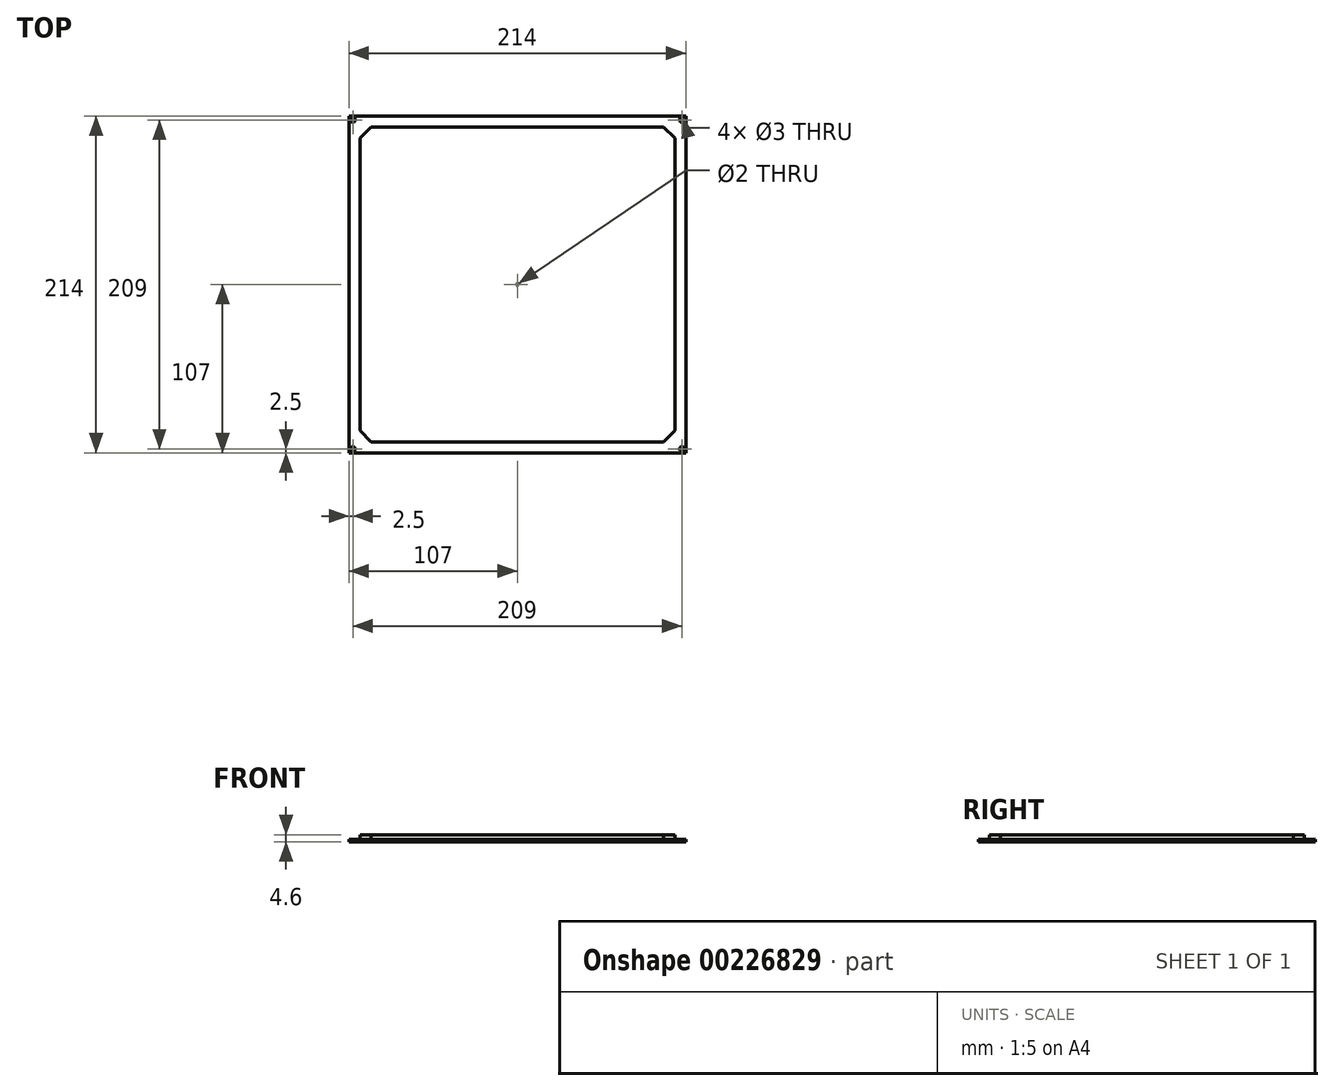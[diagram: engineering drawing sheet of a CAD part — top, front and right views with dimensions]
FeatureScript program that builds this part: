
annotation { "Feature Type Name" : "Feature", "Feature Type Description" : "" }
export const myFeature = defineFeature(function(context is Context, id is Id, definition is map)
    precondition{}
    {
        {
            var Q0;
            Q0=qCreatedBy(makeId("Top.planeOp"),FACE);
            var sketch = newSketch(context, id + "F0", { "sketchPlane" : qUnion([Q0])});
            skLineSegment(sketch, "E0.bottom", {"start": v(107, 107) * mm, "end": v(-107, 107) * mm});
            skLineSegment(sketch, "E0.top", {"start": v(107, -107) * mm, "end": v(-107, -107) * mm});
            skLineSegment(sketch, "E0.left", {"start": v(107, 107) * mm, "end": v(107, -107) * mm});
            skLineSegment(sketch, "E0.right", {"start": v(-107, 107) * mm, "end": v(-107, -107) * mm});
            skPoint(sketch, "E0.middle", {"position": v(0, 0) * mm});
            skLineSegment(sketch, "E1.bottom", {"start": v(104.5, 104.5) * mm, "end": v(-104.5, 104.5) * mm, "construction": true});
            skLineSegment(sketch, "E1.top", {"start": v(104.5, -104.5) * mm, "end": v(-104.5, -104.5) * mm, "construction": true});
            skLineSegment(sketch, "E1.left", {"start": v(104.5, 104.5) * mm, "end": v(104.5, -104.5) * mm, "construction": true});
            skLineSegment(sketch, "E1.right", {"start": v(-104.5, 104.5) * mm, "end": v(-104.5, -104.5) * mm, "construction": true});
            skCircle(sketch, "E2", {"center": v(-104.5, 104.5) * mm, "radius": 1.5 * mm});
            skCircle(sketch, "E3", {"center": v(104.5, 104.5) * mm, "radius": 1.5 * mm});
            skCircle(sketch, "E4", {"center": v(104.5, -104.5) * mm, "radius": 1.5 * mm});
            skCircle(sketch, "E5", {"center": v(-104.5, -104.5) * mm, "radius": 1.5 * mm});
            skCircle(sketch, "E6", {"center": v(0, 0) * mm, "radius": 1 * mm});
            skSolve(sketch);
        }
        {
            var Q0;
            Q0=makeQuery(id+"F0.imprint","IMPRINT",FACE,{"disambiguationData":[TD([[makeQuery(id+"F0.imprint","IMPRINT",EDGE,{"derivedFrom":sQuery(id+"F0.wireOp",EDGE,"E0.bottom")}),1.0]])]});
            extrude(context, id + "F1", {"entities" : qUnion([Q0]), "depth" : 1.6 * mm});
        }
        {
            var Q0;
            Q0=makeQuery(id+"F1.opExtrude","CAP_FACE",FACE,{"disambiguationData":[OSD([sQuery(id+"F0.wireOp",EDGE,"E0.bottom"),sQuery(id+"F0.wireOp",EDGE,"E0.top"),sQuery(id+"F0.wireOp",EDGE,"E0.left"),sQuery(id+"F0.wireOp",EDGE,"E0.right"),sQuery(id+"F0.wireOp",EDGE,"E2"),sQuery(id+"F0.wireOp",EDGE,"E3"),sQuery(id+"F0.wireOp",EDGE,"E4"),sQuery(id+"F0.wireOp",EDGE,"E5"),sQuery(id+"F0.wireOp",EDGE,"E6")])],"isStart":false});
            var sketch = newSketch(context, id + "F2", { "sketchPlane" : qUnion([Q0])});
            skLineSegment(sketch, "E7.bottom", {"start": v(92.93, 100) * mm, "end": v(-92.93, 100) * mm});
            skLineSegment(sketch, "E7.top", {"start": v(92.93, -100) * mm, "end": v(-92.93, -100) * mm});
            skLineSegment(sketch, "E7.left", {"start": v(100, 92.93) * mm, "end": v(100, -92.93) * mm});
            skLineSegment(sketch, "E7.right", {"start": v(-100, 92.93) * mm, "end": v(-100, -92.93) * mm});
            skPoint(sketch, "E7.middle", {"position": v(0, 0) * mm});
            skLineSegment(sketch, "E8", {"start": v(-100, 92.93) * mm, "end": v(-92.93, 100) * mm});
            skLineSegment(sketch, "E9", {"start": v(0, 0) * mm, "end": v(0, 100) * mm, "construction": true});
            skLineSegment(sketch, "E10", {"start": v(0, 0) * mm, "end": v(100, 0) * mm, "construction": true});
            skLineSegment(sketch, "E11.MirrorCS", {"start": v(100, 92.93) * mm, "end": v(92.93, 100) * mm});
            skLineSegment(sketch, "E12.MirrorCS", {"start": v(-100, -92.93) * mm, "end": v(-92.93, -100) * mm});
            skLineSegment(sketch, "E13.MirrorCS", {"start": v(100, -92.93) * mm, "end": v(92.93, -100) * mm});
            skPoint(sketch, "E14.orphan", {"position": v(-100, 100) * mm});
            skPoint(sketch, "E15.orphan", {"position": v(100, 100) * mm});
            skPoint(sketch, "E16.orphan", {"position": v(100, -100) * mm});
            skPoint(sketch, "E17.orphan", {"position": v(-100, -100) * mm});
            skSolve(sketch);
        }
        {
            var Q0;
            Q0=makeQuery(id+"F2.imprint","IMPRINT",FACE,{"disambiguationData":[TD([[makeQuery(id+"F2.imprint","IMPRINT",EDGE,{"derivedFrom":sQuery(id+"F2.wireOp",EDGE,"E7.bottom")}),1.0]])]});
            var Q1;
            Q1=makeQuery(id+"F2.imprint","IMPRINT",FACE,{"disambiguationData":[TD([[makeQuery(id+"F2.imprint","IMPRINT",EDGE,{"derivedFrom":makeQuery(id+"F1.opExtrude","CAP_EDGE",EDGE,{"disambiguationData":[OSD([sQuery(id+"F0.wireOp",EDGE,"E6")])],"isStart":false})}),1.0]])]});
            extrude(context, id + "F3", {"entities" : qUnion([Q0, Q1]), "depth" : 3 * mm});
        }
    });
